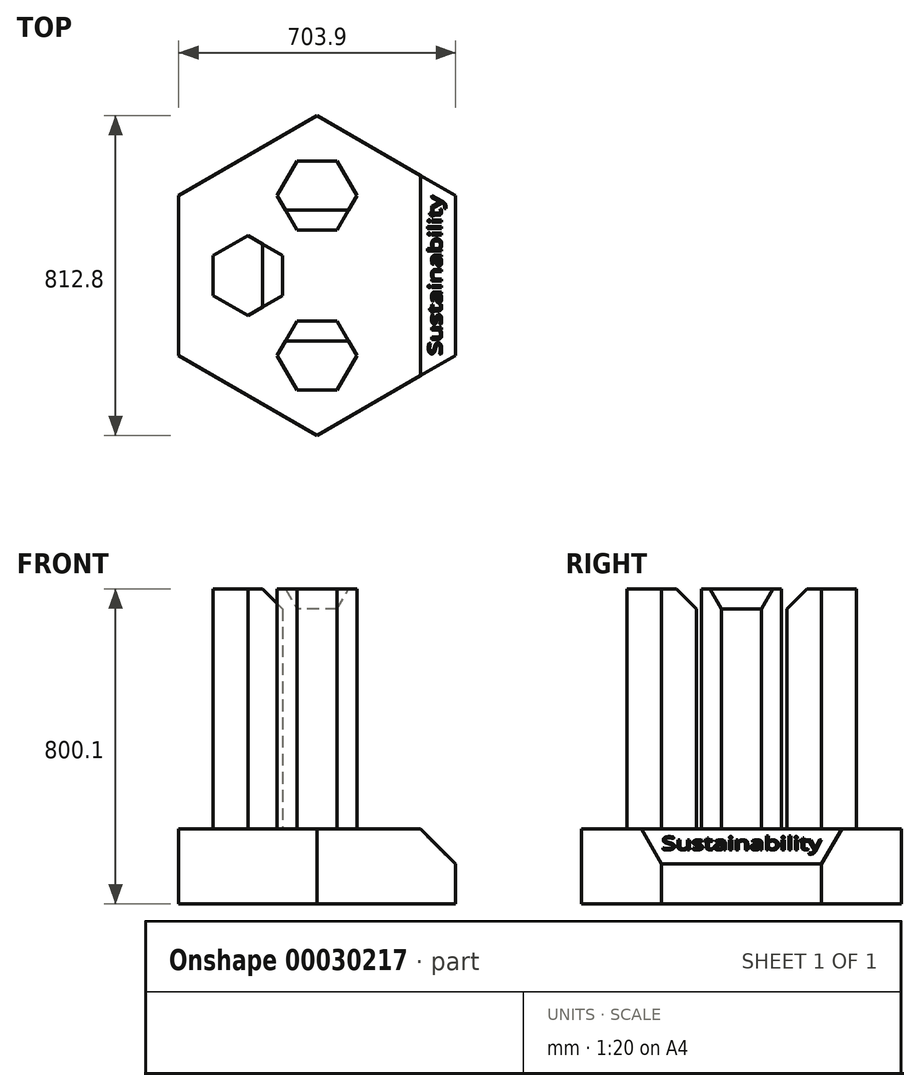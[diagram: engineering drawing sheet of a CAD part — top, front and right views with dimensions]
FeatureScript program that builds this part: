
annotation { "Feature Type Name" : "Feature", "Feature Type Description" : "" }
export const myFeature = defineFeature(function(context is Context, id is Id, definition is map)
    precondition{}
    {
        {
            var Q0;
            Q0=qCreatedBy(makeId("Top.planeOp"),FACE);
            var sketch = newSketch(context, id + "F0", { "sketchPlane" : qUnion([Q0])});
            skCircle(sketch, "E0.cCircle", {"center": v(0, 0) * mm, "radius": 351.95 * mm, "construction": true});
            skLineSegment(sketch, "E0.0", {"start": v(351.95, 203.2) * mm, "end": v(351.95, -203.2) * mm});
            skLineSegment(sketch, "E0.1", {"start": v(351.95, -203.2) * mm, "end": v(0, -406.4) * mm});
            skLineSegment(sketch, "E0.2", {"start": v(0, -406.4) * mm, "end": v(-351.95, -203.2) * mm});
            skLineSegment(sketch, "E0.3", {"start": v(-351.95, -203.2) * mm, "end": v(-351.95, 203.2) * mm});
            skLineSegment(sketch, "E0.4", {"start": v(-351.95, 203.2) * mm, "end": v(0, 406.4) * mm});
            skLineSegment(sketch, "E0.5", {"start": v(0, 406.4) * mm, "end": v(351.95, 203.2) * mm});
            skPoint(sketch, "E0.0.midPoint", {"position": v(351.95, 0) * mm});
            skSolve(sketch);
        }
        {
            var Q0;
            Q0=makeQuery(id+"F0.imprint","IMPRINT",FACE,{"disambiguationData":[TD([[makeQuery(id+"F0.imprint","IMPRINT",EDGE,{"derivedFrom":sQuery(id+"F0.wireOp",EDGE,"E0.0")}),-1.0]])]});
            extrude(context, id + "F1", {"entities" : qUnion([Q0]), "depth" : 63.5 * mm});
        }
        {
            var Q0;
            Q0=makeQuery(id+"F1.opExtrude","CAP_FACE",FACE,{"disambiguationData":[OSD([sQuery(id+"F0.wireOp",EDGE,"E0.0"),sQuery(id+"F0.wireOp",EDGE,"E0.1"),sQuery(id+"F0.wireOp",EDGE,"E0.2"),sQuery(id+"F0.wireOp",EDGE,"E0.3"),sQuery(id+"F0.wireOp",EDGE,"E0.4"),sQuery(id+"F0.wireOp",EDGE,"E0.5")])],"isStart":true});
            var sketch = newSketch(context, id + "F2", { "sketchPlane" : qUnion([Q0])});
            skCircle(sketch, "E1.cCircle", {"center": v(0, 0) * mm, "radius": 351.95 * mm, "construction": true});
            skLineSegment(sketch, "E1.0", {"start": v(351.95, 203.2) * mm, "end": v(351.95, -203.2) * mm});
            skLineSegment(sketch, "E1.1", {"start": v(351.95, -203.2) * mm, "end": v(0, -406.4) * mm});
            skLineSegment(sketch, "E1.2", {"start": v(0, -406.4) * mm, "end": v(-351.95, -203.2) * mm});
            skLineSegment(sketch, "E1.3", {"start": v(-351.95, -203.2) * mm, "end": v(-351.95, 203.2) * mm});
            skLineSegment(sketch, "E1.4", {"start": v(-351.95, 203.2) * mm, "end": v(0, 406.4) * mm});
            skLineSegment(sketch, "E1.5", {"start": v(0, 406.4) * mm, "end": v(351.95, 203.2) * mm});
            skPoint(sketch, "E1.0.midPoint", {"position": v(351.95, 0) * mm});
            skSolve(sketch);
        }
        {
            var Q0;
            Q0 = qSketchRegion(id + "F2", true);
            extrude(context, id + "F3", {"entities" : qUnion([Q0]), "operationType" : NewBodyOperationType.ADD, "depth" : 127 * mm});
        }
        {
            var Q0;
            Q0=makeQuery(id+"F1.opExtrude","CAP_EDGE",EDGE,{"disambiguationData":[OSD([sQuery(id+"F0.wireOp",EDGE,"E0.0")])],"isStart":false});
            chamfer(context, id + "F4", {"entities" : qUnion([Q0]), "width" : 88.9 * mm, "tangentPropagation" : true});
        }
        {
            var Q0;
            Q0=makeQuery(id+"F1.opExtrude","CAP_FACE",FACE,{"disambiguationData":[OSD([sQuery(id+"F0.wireOp",EDGE,"E0.0"),sQuery(id+"F0.wireOp",EDGE,"E0.1"),sQuery(id+"F0.wireOp",EDGE,"E0.2"),sQuery(id+"F0.wireOp",EDGE,"E0.3"),sQuery(id+"F0.wireOp",EDGE,"E0.4"),sQuery(id+"F0.wireOp",EDGE,"E0.5")])],"isStart":false});
            var sketch = newSketch(context, id + "F5", { "sketchPlane" : qUnion([Q0])});
            skLineSegment(sketch, "E2", {"start": v(0, -406.4) * mm, "end": v(0, 0) * mm});
            skLineSegment(sketch, "E3", {"start": v(0, 406.4) * mm, "end": v(0, 0) * mm});
            skPoint(sketch, "E4.0.midPoint", {"position": v(-87.99, 203.2) * mm});
            skLineSegment(sketch, "E5", {"start": v(-351.95, 0) * mm, "end": v(0, 0) * mm});
            skLineSegment(sketch, "E6", {"start": v(-351.95, 0) * mm, "end": v(-175.98, 0) * mm});
            skCircle(sketch, "E7.cCircle", {"center": v(-175.98, 0) * mm, "radius": 87.99 * mm, "construction": true});
            skLineSegment(sketch, "E7.0", {"start": v(-87.99, 50.8) * mm, "end": v(-87.99, -50.8) * mm});
            skLineSegment(sketch, "E7.1", {"start": v(-87.99, -50.8) * mm, "end": v(-175.98, -101.6) * mm});
            skLineSegment(sketch, "E7.2", {"start": v(-175.98, -101.6) * mm, "end": v(-263.96, -50.8) * mm});
            skLineSegment(sketch, "E7.3", {"start": v(-263.96, -50.8) * mm, "end": v(-263.96, 50.8) * mm});
            skLineSegment(sketch, "E7.4", {"start": v(-263.96, 50.8) * mm, "end": v(-175.98, 101.6) * mm});
            skLineSegment(sketch, "E7.5", {"start": v(-175.98, 101.6) * mm, "end": v(-87.99, 50.8) * mm});
            skLineSegment(sketch, "E8", {"start": v(0, -406.4) * mm, "end": v(0, -203.2) * mm});
            skLineSegment(sketch, "E9", {"start": v(0, -203.2) * mm, "end": v(0, 203.2) * mm});
            skCircle(sketch, "E10.cCircle", {"center": v(0, 203.2) * mm, "radius": 87.99 * mm, "construction": true});
            skLineSegment(sketch, "E10.0", {"start": v(-50.8, 291.19) * mm, "end": v(50.8, 291.19) * mm});
            skLineSegment(sketch, "E10.1", {"start": v(50.8, 291.19) * mm, "end": v(101.6, 203.2) * mm});
            skLineSegment(sketch, "E10.2", {"start": v(101.6, 203.2) * mm, "end": v(50.8, 115.21) * mm});
            skLineSegment(sketch, "E10.3", {"start": v(50.8, 115.21) * mm, "end": v(-50.8, 115.21) * mm});
            skLineSegment(sketch, "E10.4", {"start": v(-50.8, 115.21) * mm, "end": v(-101.6, 203.2) * mm});
            skLineSegment(sketch, "E10.5", {"start": v(-101.6, 203.2) * mm, "end": v(-50.8, 291.19) * mm});
            skPoint(sketch, "E10.0.midPoint", {"position": v(0, 291.19) * mm});
            skCircle(sketch, "E11.cCircle", {"center": v(0, -203.2) * mm, "radius": 87.99 * mm, "construction": true});
            skLineSegment(sketch, "E11.0", {"start": v(-50.8, -115.21) * mm, "end": v(50.8, -115.21) * mm});
            skLineSegment(sketch, "E11.1", {"start": v(50.8, -115.21) * mm, "end": v(101.6, -203.2) * mm});
            skLineSegment(sketch, "E11.2", {"start": v(101.6, -203.2) * mm, "end": v(50.8, -291.19) * mm});
            skLineSegment(sketch, "E11.3", {"start": v(50.8, -291.19) * mm, "end": v(-50.8, -291.19) * mm});
            skLineSegment(sketch, "E11.4", {"start": v(-50.8, -291.19) * mm, "end": v(-101.6, -203.2) * mm});
            skLineSegment(sketch, "E11.5", {"start": v(-101.6, -203.2) * mm, "end": v(-50.8, -115.21) * mm});
            skPoint(sketch, "E11.0.midPoint", {"position": v(0, -115.21) * mm});
            skSolve(sketch);
        }
        {
            var Q0;
            Q0=makeQuery(id+"F5.imprint","IMPRINT",FACE,{"disambiguationData":[TD([[makeQuery(id+"F5.imprint","IMPRINT",EDGE,{"derivedFrom":sQuery(id+"F5.wireOp",EDGE,"5c5648d7-171f-4d33-9fea-e2935a9d3056.0")}),-1.0]])]});
            var Q1;
            {var subQ1=sQuery(id+"F5.wireOp",EDGE,"5c5648d7-171f-4d33-9fea-e2935a9d3056.2");Q1=makeQuery(id+"F5.imprint","IMPRINT",FACE,{"disambiguationData":[TD([[makeQuery(id+"F5.imprint","IMPRINT",EDGE,{"derivedFrom":subQ1}),-1.0]])]});}
            var Q2;
            {var subQ4=sQuery(id+"F5.wireOp",EDGE,"E7.1");Q2=makeQuery(id+"F5.imprint","IMPRINT",FACE,{"disambiguationData":[TD([[makeQuery(id+"F5.imprint","IMPRINT",EDGE,{"derivedFrom":subQ4}),-1.0]])]});}
            var Q3;
            {var subQ1=sQuery(id+"F5.wireOp",EDGE,"E7.4");Q3=makeQuery(id+"F5.imprint","IMPRINT",FACE,{"disambiguationData":[TD([[makeQuery(id+"F5.imprint","IMPRINT",EDGE,{"derivedFrom":subQ1}),-1.0]])]});}
            var Q4;
            Q4=makeQuery(id+"F5.imprint","IMPRINT",FACE,{"disambiguationData":[TD([[makeQuery(id+"F5.imprint","IMPRINT",EDGE,{"derivedFrom":sQuery(id+"F5.wireOp",EDGE,"E4.0")}),-1.0]])]});
            var Q5;
            {var subQ1=sQuery(id+"F5.wireOp",EDGE,"E4.2");Q5=makeQuery(id+"F5.imprint","IMPRINT",FACE,{"disambiguationData":[TD([[makeQuery(id+"F5.imprint","IMPRINT",EDGE,{"derivedFrom":subQ1}),-1.0]])]});}
            extrude(context, id + "F6", {"entities" : qUnion([Q0, Q1, Q2, Q3, Q4, Q5]), "operationType" : NewBodyOperationType.ADD, "depth" : 609.6 * mm});
        }
        {
            var Q0;
            Q0 = qSketchRegion(id + "F5", true);
            extrude(context, id + "F7", {"entities" : qUnion([Q0]), "operationType" : NewBodyOperationType.ADD, "depth" : 609.6 * mm});
        }
        {
            var Q0;
            Q0=makeQuery(id+"F7.opExtrude","CAP_EDGE",EDGE,{"disambiguationData":[OSD([sQuery(id+"F5.wireOp",EDGE,"E11.0")])],"isStart":false});
            var Q1;
            Q1=makeQuery(id+"F6.opExtrude","CAP_EDGE",EDGE,{"disambiguationData":[OSD([sQuery(id+"F5.wireOp",EDGE,"E7.0")])],"isStart":false});
            var Q2;
            Q2=makeQuery(id+"F7.opExtrude","CAP_EDGE",EDGE,{"disambiguationData":[OSD([sQuery(id+"F5.wireOp",EDGE,"E10.3")])],"isStart":false});
            chamfer(context, id + "F8", {"entities" : qUnion([Q0, Q1, Q2]), "width" : 50.8 * mm, "tangentPropagation" : true});
        }
        {
            var Q0;
            Q0=makeQuery(id+"F4.opChamfer","BLEND_FACE",FACE,{"disambiguationData":[OSD([sQuery(id+"F0.wireOp",EDGE,"E0.0")])]});
            var sketch = newSketch(context, id + "F9", { "sketchPlane" : qUnion([Q0])});
            skText(sketch, "E12", { "text": "Sustainability\n", "fontName": "OpenSans-Regular.ttf"});
            const initialGuessF9  = {"E12": [-0.20318, -0.21603, 1, 0, 0.0472]};
            skSetInitialGuess(sketch, initialGuessF9);
            skSolve(sketch);
        }
        {
            var Q0;
            Q0 = qSketchRegion(id + "F9", true);
            extrude(context, id + "F10", {"entities" : qUnion([Q0]), "operationType" : NewBodyOperationType.REMOVE, "oppositeDirection" : true, "depth" : 2.54 * mm});
        }
    });
